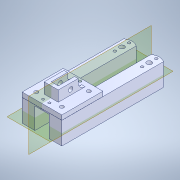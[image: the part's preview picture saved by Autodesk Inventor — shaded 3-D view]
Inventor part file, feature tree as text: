
AUTODESK INVENTOR PART (.ipt)
format: ipt  version: 2022 (Build 260153000, 153)  size: 320,512 bytes
history: mixed  units: in
note: dims shown in document units (in); Inventor stores cm internally (conversion verified against a paired STEP export)
features: move_body x12, reference x6, other x4, direct_edit x3, extrude x3, sketch x3, plane x2, imported_body x1
ambient origin geometry x8: Origin, YZ Plane, XZ Plane, XY Plane, X Axis, Y Axis, Z Axis, Center Point
bodies: Solid1 (imported_parasolid), Solid2 (imported_parasolid)
feature tree (34):
  plane  "Work Plane1"
  plane  "Work Plane2"
  direct_edit  "Direct Edit1"
  extrude  "Extrusion1"  TaperAngle=0.0deg  [1 undecoded]
  direct_edit  "Direct Edit3"
  direct_edit  "Direct Edit4"
  extrude  "Extrusion2"  TaperAngle=0.0deg  [1 undecoded]
  extrude  "Extrusion3"  TaperAngle=0.0deg  [1 undecoded]
  sketch  "Sketch1"  dims[d0=0.0in d1=0.0in d2=-0.4252in d3=0.0in d4=-0.4252in d5=0.0in]
  sketch  "Sketch2"  dims[d6=0.0in d7=-0.4252in d8=0.0in d9=0.0in d10=-0.4252in d11=0.0in]
  reference  "Reference1"
  reference  "Reference2"
  reference  "Reference3"
  sketch  "Sketch3"  dims[d12=0.0in d13=-0.4252in d14=0.0in d15=0.0in d16=0.0in d17=-0.4252in d18=0.3937in d19=0.0in d29=0.0in d30=0.0in d31=0.4252in d32=0.0in d33=0.0in d34=0.4252in d35=0.0in d36=0.0in d37=-0.4252in d38=0.0in d39=0.0in d40=0.4252in d41=0.0in d42=0.0in d43=-0.4252in d44=0.0in d45=-0.4252in d46=0.0in d47=0.0039in d48=0.0039in d49=0.1535in d50=0.1535in d51=0.3937in d52=0.0in d53=0.0394in d54=0.1535in d55=0.1535in d56=0.3937in d57=0.0in]
  reference  "Reference4"
  reference  "Reference5"
  reference  "Reference6"
  other  "Actuator coupler:1"
  other  "Actuator servo holder:1"
  move_body  "Move1"
  move_body  "Move2"
  move_body  "Move3"
  move_body  "Move4"
  move_body  "Move5"
  move_body  "Move6"
  move_body  "Move10"
  move_body  "Move11"
  move_body  "Move12"
  move_body  "Move13"
  move_body  "Move14"
  move_body  "Move15"
  other  "Servo head assembly.iam"
  other  "big servo:1"
  imported_body  NMx_Import_Brep_tag  [imported B-rep: ~75 faces, bbox_mm=[56.0, 53.1, 144.149061]]
note: 3 required parameter values undecoded (feature->parameter linkage not recoverable at this tier; creation-order binding heuristic only, values carry confidence <= 0.55)
